AUTODESK INVENTOR PART (.ipt)
format: ipt  version: 2024 (Build 280153000, 153)  size: 149,504 bytes
history: native  units: mm (DEFAULTED — no unit token found)
features: other x4, extrude x2, sketch x2, plane x1
ambient origin geometry x8: Origin, YZ Plane, XZ Plane, XY Plane, X Axis, Y Axis, Z Axis, Center Point
bodies: Solid1 (feature_tree)
feature tree (9):
  parser-record x1  (decoder bookkeeping rows leaked as tree rows — omitted from the tree; the rows remain in map.json)
  other  "Driven Length"
  other  "Plano inicial"
  other  "Plano final"
  extrude  "Cuerpo"  TaperAngle=0.0deg  [1 undecoded]
  extrude  "Extrusión2"  Depth=50.8mm
  sketch  "Sketch3"  dims[d3=2190.0mm d4=0.0mm]
  plane  "Work Plane3"
  sketch  "Boceto5"  dims[d10=50.8mm d11=50.8mm d12=3.175mm d13=-0.0mm d14=2190.0mm d15=25.4mm d16=25.4mm d17=6.35mm d18=90.0deg d19=2190.0mm d20=18.034mm d21=18.034mm d22=18.034mm d23=1651.0mm d24=863.6mm d25=95.1484mm d26=19.05mm d27=0.0mm]
note: 1 required parameter value undecoded (feature->parameter linkage not recoverable at this tier; creation-order binding heuristic only, values carry confidence <= 0.55)
